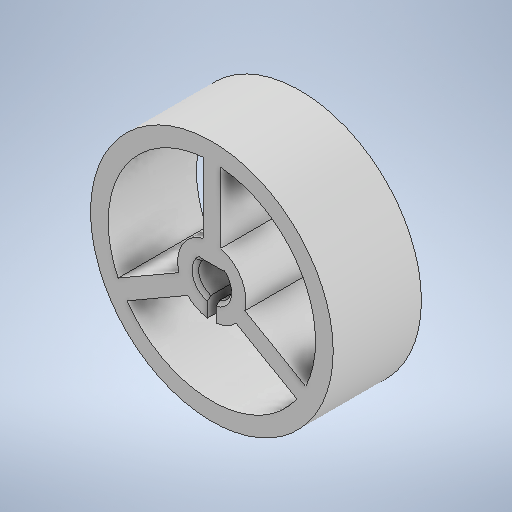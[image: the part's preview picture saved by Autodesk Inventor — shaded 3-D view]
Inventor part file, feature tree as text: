
AUTODESK INVENTOR PART (.ipt)
format: ipt  version: 2025.3 (Build 293356000, 356)  size: 313,856 bytes
history: native  units: mm
features: other x1, extrude x1, pattern_circular x1, chamfer x1
ambient origin geometry x8: Origin, YZ Plane, XZ Plane, XY Plane, X Axis, Y Axis, Z Axis, Center Point
bodies: Body1 (feature_tree)
feature tree (4):
  other  "ソリッド1"
  extrude  "スポーク"  Depth=1.05mm
  pattern_circular  "円形状パターン1"  [2 undecoded]
  chamfer  "面取り1"  Distance=8.0mm
note: 2 required parameter values undecoded (feature->parameter linkage not recoverable at this tier; creation-order binding heuristic only, values carry confidence <= 0.55)
